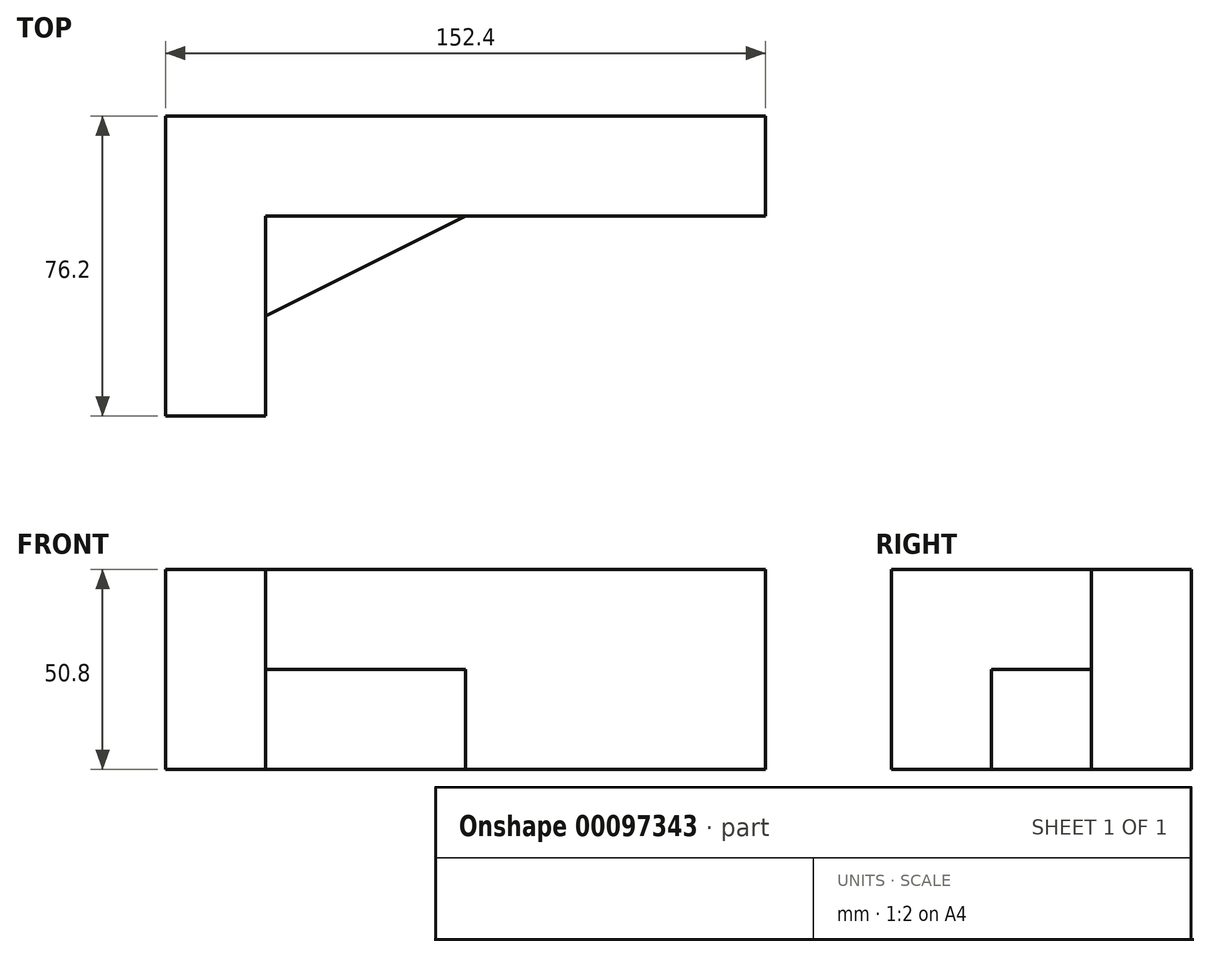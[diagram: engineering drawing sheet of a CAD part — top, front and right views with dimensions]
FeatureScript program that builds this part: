
annotation { "Feature Type Name" : "Feature", "Feature Type Description" : "" }
export const myFeature = defineFeature(function(context is Context, id is Id, definition is map)
    precondition{}
    {
        {
            var Q0;
            Q0=qCreatedBy(makeId("Top.planeOp"),FACE);
            var sketch = newSketch(context, id + "F0", { "sketchPlane" : qUnion([Q0])});
            skLineSegment(sketch, "E0", {"start": v(0, 0) * mm, "end": v(0, 76.2) * mm});
            skLineSegment(sketch, "E1", {"start": v(0, 76.2) * mm, "end": v(152.4, 76.2) * mm});
            skLineSegment(sketch, "E2", {"start": v(152.4, 76.2) * mm, "end": v(152.4, 50.8) * mm});
            skLineSegment(sketch, "E3", {"start": v(152.4, 50.8) * mm, "end": v(25.4, 50.8) * mm});
            skLineSegment(sketch, "E4", {"start": v(25.4, 50.8) * mm, "end": v(25.4, 0) * mm});
            skLineSegment(sketch, "E5", {"start": v(25.4, 0) * mm, "end": v(0, 0) * mm});
            skSolve(sketch);
        }
        {
            var Q0;
            Q0=makeQuery(id+"F0.imprint","IMPRINT",FACE,{"disambiguationData":[TD([[makeQuery(id+"F0.imprint","IMPRINT",EDGE,{"derivedFrom":sQuery(id+"F0.wireOp",EDGE,"E0")}),-1.0]])]});
            extrude(context, id + "F1", {"entities" : qUnion([Q0]), "depth" : 50.8 * mm});
        }
        {
            var Q0;
            Q0=qCreatedBy(makeId("Top.planeOp"),FACE);
            var sketch = newSketch(context, id + "F2", { "sketchPlane" : qUnion([Q0])});
            skLineSegment(sketch, "E6.0", {"start": v(25.4, 50.8) * mm, "end": v(25.4, 0) * mm});
            skLineSegment(sketch, "E7.0", {"start": v(152.4, 50.8) * mm, "end": v(25.4, 50.8) * mm});
            skLineSegment(sketch, "E8", {"start": v(25.4, 25.4) * mm, "end": v(76.2, 50.8) * mm});
            skSolve(sketch);
        }
        {
            var Q0;
            {var subQ3=sQuery(id+"F2.wireOp",EDGE,"E8");Q0=makeQuery(id+"F2.imprint","IMPRINT",FACE,{"disambiguationData":[TD([[makeQuery(id+"F2.imprint","IMPRINT",EDGE,{"derivedFrom":subQ3}),1.0]])]});}
            extrude(context, id + "F3", {"entities" : qUnion([Q0]), "operationType" : NewBodyOperationType.ADD, "depth" : 25.4 * mm});
        }
    });
